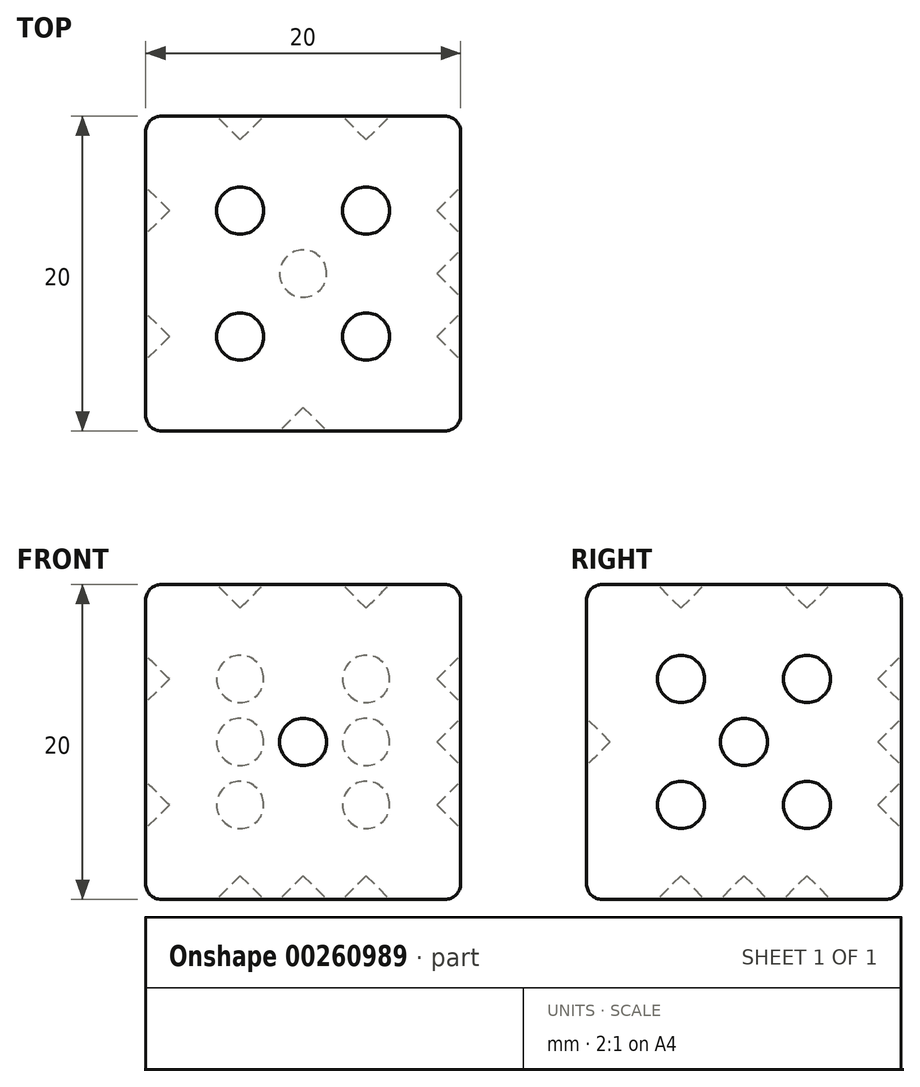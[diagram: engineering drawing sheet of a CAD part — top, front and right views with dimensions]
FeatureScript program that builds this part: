
annotation { "Feature Type Name" : "Feature", "Feature Type Description" : "" }
export const myFeature = defineFeature(function(context is Context, id is Id, definition is map)
    precondition{}
    {
        {
            var Q0;
            Q0=qCreatedBy(makeId("Top.planeOp"),FACE);
            var sketch = newSketch(context, id + "F0", { "sketchPlane" : qUnion([Q0])});
            skLineSegment(sketch, "E0.bottom", {"start": v(0, 0) * mm, "end": v(20, 0) * mm});
            skLineSegment(sketch, "E0.top", {"start": v(0, 20) * mm, "end": v(20, 20) * mm});
            skLineSegment(sketch, "E0.left", {"start": v(0, 0) * mm, "end": v(0, 20) * mm});
            skLineSegment(sketch, "E0.right", {"start": v(20, 0) * mm, "end": v(20, 20) * mm});
            skSolve(sketch);
        }
        {
            var Q0;
            Q0 = qSketchRegion(id + "F0", true);
            extrude(context, id + "F1", {"entities" : qUnion([Q0]), "depth" : 20 * mm});
        }
        {
            var Q0;
            Q0=makeQuery(id+"F1.opExtrude","SWEPT_FACE",FACE,{"disambiguationData":[OSD([sQuery(id+"F0.wireOp",EDGE,"E0.bottom")])]});
            var sketch = newSketch(context, id + "F2", { "sketchPlane" : qUnion([Q0])});
            skLineSegment(sketch, "E1.0", {"start": v(0, 20) * mm, "end": v(20, 20) * mm, "construction": true});
            skLineSegment(sketch, "E1.1", {"start": v(0, 0) * mm, "end": v(20, 0) * mm, "construction": true});
            skLineSegment(sketch, "E2", {"start": v(10, 20) * mm, "end": v(10, 0) * mm, "construction": true});
            skCircle(sketch, "E3", {"center": v(10, 10) * mm, "radius": 1.5 * mm});
            skSolve(sketch);
        }
        {
            var Q0;
            Q0=makeQuery(id+"F2.imprint","IMPRINT",FACE,{"disambiguationData":[TD([[makeQuery(id+"F2.imprint","IMPRINT",EDGE,{"derivedFrom":sQuery(id+"F2.wireOp",EDGE,"E3")}),1.0]])]});
            var Q1;
            Q1=sQuery(id+"F2.wireOp",EDGE,"E3");
            extrude(context, id + "F3", {"entities" : qUnion([Q0]), "operationType" : NewBodyOperationType.REMOVE, "surfaceEntities" : qUnion([Q1]), "oppositeDirection" : true, "depth" : 1.5 * mm});
        }
        {
            var Q0;
            Q0=makeQuery(id+"F1.opExtrude","CAP_FACE",FACE,{"disambiguationData":[OSD([sQuery(id+"F0.wireOp",EDGE,"E0.bottom"),sQuery(id+"F0.wireOp",EDGE,"E0.top"),sQuery(id+"F0.wireOp",EDGE,"E0.left"),sQuery(id+"F0.wireOp",EDGE,"E0.right")])],"isStart":false});
            var sketch = newSketch(context, id + "F4", { "sketchPlane" : qUnion([Q0])});
            skLineSegment(sketch, "E4.0", {"start": v(0, 20) * mm, "end": v(6, 20) * mm, "construction": true});
            skLineSegment(sketch, "E5", {"start": v(6, 20) * mm, "end": v(6, 14) * mm, "construction": true});
            skCircle(sketch, "E6", {"center": v(6, 14) * mm, "radius": 1.5 * mm});
            skCircle(sketch, "E7", {"center": v(6, 6) * mm, "radius": 1.5 * mm});
            skPoint(sketch, "E8.orphan", {"position": v(20, 0) * mm});
            skPoint(sketch, "E9.orphan", {"position": v(20, 20) * mm});
            skLineSegment(sketch, "E10", {"start": v(0, 0) * mm, "end": v(6, 0) * mm, "construction": true});
            skLineSegment(sketch, "E11", {"start": v(6, 0) * mm, "end": v(6, 6) * mm, "construction": true});
            skLineSegment(sketch, "E12.0", {"start": v(0, 20) * mm, "end": v(20, 20) * mm, "construction": true});
            skLineSegment(sketch, "E12.1", {"start": v(0, 0) * mm, "end": v(20, 0) * mm, "construction": true});
            skLineSegment(sketch, "E13", {"start": v(10, 20) * mm, "end": v(10, 0) * mm, "construction": true});
            skCircle(sketch, "E14.MirrorC", {"center": v(14, 6) * mm, "radius": 1.5 * mm});
            skCircle(sketch, "E15.MirrorC", {"center": v(14, 14) * mm, "radius": 1.5 * mm});
            skSolve(sketch);
        }
        {
            var Q0;
            Q0 = qSketchRegion(id + "F4", true);
            extrude(context, id + "F5", {"entities" : qUnion([Q0]), "operationType" : NewBodyOperationType.REMOVE, "oppositeDirection" : true, "depth" : 1.5 * mm});
        }
        {
            var Q0;
            Q0=makeQuery(id+"F1.opExtrude","SWEPT_FACE",FACE,{"disambiguationData":[OSD([sQuery(id+"F0.wireOp",EDGE,"E0.right")])]});
            var sketch = newSketch(context, id + "F6", { "sketchPlane" : qUnion([Q0])});
            skLineSegment(sketch, "E16", {"start": v(0, 20) * mm, "end": v(6, 20) * mm, "construction": true});
            skLineSegment(sketch, "E17", {"start": v(6, 20) * mm, "end": v(6, 14) * mm, "construction": true});
            skLineSegment(sketch, "E18", {"start": v(0, 0) * mm, "end": v(6, 0) * mm, "construction": true});
            skLineSegment(sketch, "E19", {"start": v(6, 0) * mm, "end": v(6, 6) * mm, "construction": true});
            skCircle(sketch, "E20", {"center": v(6, 14) * mm, "radius": 1.5 * mm});
            skCircle(sketch, "E21", {"center": v(6, 6) * mm, "radius": 1.5 * mm});
            skLineSegment(sketch, "E22", {"start": v(0, 20) * mm, "end": v(10, 20) * mm, "construction": true});
            skLineSegment(sketch, "E23", {"start": v(10, 20) * mm, "end": v(10, 0) * mm, "construction": true});
            skCircle(sketch, "E24.MirrorC", {"center": v(14, 6) * mm, "radius": 1.5 * mm});
            skCircle(sketch, "E25.MirrorC", {"center": v(14, 14) * mm, "radius": 1.5 * mm});
            skCircle(sketch, "E26", {"center": v(10, 10) * mm, "radius": 1.5 * mm});
            skSolve(sketch);
        }
        {
            var Q0;
            Q0 = qSketchRegion(id + "F6", true);
            extrude(context, id + "F7", {"entities" : qUnion([Q0]), "operationType" : NewBodyOperationType.REMOVE, "oppositeDirection" : true, "depth" : 1.5 * mm});
        }
        {
            var Q0;
            Q0=makeQuery(id+"F1.opExtrude","SWEPT_FACE",FACE,{"disambiguationData":[OSD([sQuery(id+"F0.wireOp",EDGE,"E0.top")])]});
            var sketch = newSketch(context, id + "F8", { "sketchPlane" : qUnion([Q0])});
            skLineSegment(sketch, "E27", {"start": v(-20, 20) * mm, "end": v(-14, 20) * mm, "construction": true});
            skLineSegment(sketch, "E28", {"start": v(-14, 20) * mm, "end": v(-14, 14) * mm, "construction": true});
            skLineSegment(sketch, "E29", {"start": v(-20, 0) * mm, "end": v(-14, 0) * mm, "construction": true});
            skLineSegment(sketch, "E30", {"start": v(-14, 0) * mm, "end": v(-14, 6) * mm, "construction": true});
            skLineSegment(sketch, "E31", {"start": v(-20, 20) * mm, "end": v(-14, 20) * mm});
            skLineSegment(sketch, "E32", {"start": v(-20, 0) * mm, "end": v(-14, 0) * mm});
            skCircle(sketch, "E33", {"center": v(-14, 14) * mm, "radius": 1.5 * mm});
            skCircle(sketch, "E34", {"center": v(-14, 6) * mm, "radius": 1.5 * mm});
            skLineSegment(sketch, "E35", {"start": v(-14, 14) * mm, "end": v(-14, 6) * mm, "construction": true});
            skCircle(sketch, "E36", {"center": v(-14, 10) * mm, "radius": 1.5 * mm});
            skLineSegment(sketch, "E37", {"start": v(-20, 20) * mm, "end": v(-10, 20) * mm, "construction": true});
            skLineSegment(sketch, "E38", {"start": v(-10, 20) * mm, "end": v(-10, 0) * mm, "construction": true});
            skCircle(sketch, "E39.MirrorC", {"center": v(-6, 14) * mm, "radius": 1.5 * mm});
            skCircle(sketch, "E40.MirrorC", {"center": v(-6, 10) * mm, "radius": 1.5 * mm});
            skCircle(sketch, "E41.MirrorC", {"center": v(-6, 6) * mm, "radius": 1.5 * mm});
            skSolve(sketch);
        }
        {
            var Q0;
            Q0 = qSketchRegion(id + "F8", true);
            extrude(context, id + "F9", {"entities" : qUnion([Q0]), "operationType" : NewBodyOperationType.REMOVE, "oppositeDirection" : true, "depth" : 1.5 * mm});
        }
        {
            var Q0;
            Q0=makeQuery(id+"F1.opExtrude","SWEPT_FACE",FACE,{"disambiguationData":[OSD([sQuery(id+"F0.wireOp",EDGE,"E0.left")])]});
            var sketch = newSketch(context, id + "F10", { "sketchPlane" : qUnion([Q0])});
            skLineSegment(sketch, "E42", {"start": v(-20, 20) * mm, "end": v(-14, 20) * mm, "construction": true});
            skLineSegment(sketch, "E43", {"start": v(-14, 20) * mm, "end": v(-14, 14) * mm, "construction": true});
            skCircle(sketch, "E44", {"center": v(-14, 14) * mm, "radius": 1.5 * mm});
            skLineSegment(sketch, "E45", {"start": v(-20, 0) * mm, "end": v(0, 20) * mm, "construction": true});
            skCircle(sketch, "E46.MirrorC", {"center": v(-6, 6) * mm, "radius": 1.5 * mm});
            skSolve(sketch);
        }
        {
            var Q0;
            Q0 = qSketchRegion(id + "F10", true);
            extrude(context, id + "F11", {"entities" : qUnion([Q0]), "operationType" : NewBodyOperationType.REMOVE, "oppositeDirection" : true, "depth" : 1.5 * mm});
        }
        {
            var Q0;
            Q0=makeQuery(id+"F1.opExtrude","CAP_FACE",FACE,{"disambiguationData":[OSD([sQuery(id+"F0.wireOp",EDGE,"E0.bottom"),sQuery(id+"F0.wireOp",EDGE,"E0.top"),sQuery(id+"F0.wireOp",EDGE,"E0.left"),sQuery(id+"F0.wireOp",EDGE,"E0.right")])],"isStart":true});
            var sketch = newSketch(context, id + "F12", { "sketchPlane" : qUnion([Q0])});
            skLineSegment(sketch, "E47", {"start": v(0, 0) * mm, "end": v(6, 0) * mm, "construction": true});
            skLineSegment(sketch, "E48", {"start": v(6, 0) * mm, "end": v(6, -6) * mm, "construction": true});
            skCircle(sketch, "E49", {"center": v(6, -6) * mm, "radius": 1.5 * mm});
            skLineSegment(sketch, "E50", {"start": v(0, -20) * mm, "end": v(20, 0) * mm, "construction": true});
            skCircle(sketch, "E51.MirrorC", {"center": v(14, -14) * mm, "radius": 1.5 * mm});
            skCircle(sketch, "E52", {"center": v(10, -10) * mm, "radius": 1.5 * mm});
            skSolve(sketch);
        }
        {
            var Q0;
            Q0 = qSketchRegion(id + "F12", true);
            extrude(context, id + "F13", {"entities" : qUnion([Q0]), "operationType" : NewBodyOperationType.REMOVE, "oppositeDirection" : true, "depth" : 1.5 * mm});
        }
        {
            var Q0;
            Q0=makeQuery(id+"F1.opExtrude","CAP_EDGE",EDGE,{"disambiguationData":[OSD([sQuery(id+"F0.wireOp",EDGE,"E0.left")])],"isStart":false});
            var Q1;
            Q1=makeQuery(id+"F1.opExtrude","CAP_EDGE",EDGE,{"disambiguationData":[OSD([sQuery(id+"F0.wireOp",EDGE,"E0.right")])],"isStart":false});
            var Q2;
            Q2=makeQuery(id+"F1.opExtrude","CAP_EDGE",EDGE,{"disambiguationData":[OSD([sQuery(id+"F0.wireOp",EDGE,"E0.bottom")])],"isStart":false});
            var Q3;
            Q3=makeQuery(id+"F1.opExtrude","CAP_EDGE",EDGE,{"disambiguationData":[OSD([sQuery(id+"F0.wireOp",EDGE,"E0.bottom")])],"isStart":true});
            var Q4;
            Q4=makeQuery(id+"F1.opExtrude","CAP_EDGE",EDGE,{"disambiguationData":[OSD([sQuery(id+"F0.wireOp",EDGE,"E0.left")])],"isStart":true});
            var Q5;
            Q5=makeQuery(id+"F1.opExtrude","CAP_EDGE",EDGE,{"disambiguationData":[OSD([sQuery(id+"F0.wireOp",EDGE,"E0.top")])],"isStart":true});
            var Q6;
            Q6=makeQuery(id+"F1.opExtrude","CAP_EDGE",EDGE,{"disambiguationData":[OSD([sQuery(id+"F0.wireOp",EDGE,"E0.top")])],"isStart":false});
            var Q7;
            Q7=makeQuery(id+"F1.opExtrude","SWEPT_EDGE",EDGE,{"disambiguationData":[OSD([sQuery(id+"F0.wireOp",EDGE,"E0.top"),sQuery(id+"F0.wireOp",EDGE,"E0.right")])]});
            var Q8;
            Q8=makeQuery(id+"F1.opExtrude","SWEPT_EDGE",EDGE,{"disambiguationData":[OSD([sQuery(id+"F0.wireOp",EDGE,"E0.top"),sQuery(id+"F0.wireOp",EDGE,"E0.left")])]});
            var Q9;
            Q9=makeQuery(id+"F1.opExtrude","SWEPT_EDGE",EDGE,{"disambiguationData":[OSD([sQuery(id+"F0.wireOp",EDGE,"E0.bottom"),sQuery(id+"F0.wireOp",EDGE,"E0.right")])]});
            var Q10;
            Q10=makeQuery(id+"F1.opExtrude","SWEPT_EDGE",EDGE,{"disambiguationData":[OSD([sQuery(id+"F0.wireOp",EDGE,"E0.bottom"),sQuery(id+"F0.wireOp",EDGE,"E0.left")])]});
            var Q11;
            Q11=makeQuery(id+"F1.opExtrude","CAP_EDGE",EDGE,{"disambiguationData":[OSD([sQuery(id+"F0.wireOp",EDGE,"E0.right")])],"isStart":true});
            fillet(context, id + "F14", {"entities" : qUnion([Q0, Q1, Q2, Q3, Q4, Q5, Q6, Q7, Q8, Q9, Q10, Q11]), "radius" : 1 * mm, "tangentPropagation" : true, "allowEdgeOverflow" : false});
        }
        {
            var Q0;
            Q0=makeQuery(id+"F3.boolean.opBoolean","COPY",EDGE,{"derivedFrom":makeQuery(id+"F3.opExtrude","CAP_EDGE",EDGE,{"disambiguationData":[OSD([sQuery(id+"F2.wireOp",EDGE,"E3")])],"isStart":false})});
            var Q1;
            Q1=makeQuery(id+"F5.boolean.opBoolean","COPY",EDGE,{"derivedFrom":makeQuery(id+"F5.opExtrude","CAP_EDGE",EDGE,{"disambiguationData":[OSD([sQuery(id+"F4.wireOp",EDGE,"E6")])],"isStart":false})});
            var Q2;
            Q2=makeQuery(id+"F5.boolean.opBoolean","COPY",EDGE,{"derivedFrom":makeQuery(id+"F5.opExtrude","CAP_EDGE",EDGE,{"disambiguationData":[OSD([sQuery(id+"F4.wireOp",EDGE,"E7")])],"isStart":false})});
            var Q3;
            Q3=makeQuery(id+"F5.boolean.opBoolean","COPY",EDGE,{"derivedFrom":makeQuery(id+"F5.opExtrude","CAP_EDGE",EDGE,{"disambiguationData":[OSD([sQuery(id+"F4.wireOp",EDGE,"E14.MirrorC")])],"isStart":false})});
            var Q4;
            Q4=makeQuery(id+"F5.boolean.opBoolean","COPY",EDGE,{"derivedFrom":makeQuery(id+"F5.opExtrude","CAP_EDGE",EDGE,{"disambiguationData":[OSD([sQuery(id+"F4.wireOp",EDGE,"E15.MirrorC")])],"isStart":false})});
            var Q5;
            Q5=makeQuery(id+"F7.boolean.opBoolean","COPY",FACE,{"derivedFrom":makeQuery(id+"F7.opExtrude","CAP_FACE",FACE,{"disambiguationData":[OSD([sQuery(id+"F6.wireOp",EDGE,"E21")])],"isStart":false})});
            var Q6;
            Q6=makeQuery(id+"F7.boolean.opBoolean","COPY",FACE,{"derivedFrom":makeQuery(id+"F7.opExtrude","CAP_FACE",FACE,{"disambiguationData":[OSD([sQuery(id+"F6.wireOp",EDGE,"E20")])],"isStart":false})});
            var Q7;
            Q7=makeQuery(id+"F7.boolean.opBoolean","COPY",FACE,{"derivedFrom":makeQuery(id+"F7.opExtrude","CAP_FACE",FACE,{"disambiguationData":[OSD([sQuery(id+"F6.wireOp",EDGE,"E25.MirrorC")])],"isStart":false})});
            var Q8;
            Q8=makeQuery(id+"F7.boolean.opBoolean","COPY",FACE,{"derivedFrom":makeQuery(id+"F7.opExtrude","CAP_FACE",FACE,{"disambiguationData":[OSD([sQuery(id+"F6.wireOp",EDGE,"E24.MirrorC")])],"isStart":false})});
            var Q9;
            Q9=makeQuery(id+"F7.boolean.opBoolean","COPY",FACE,{"derivedFrom":makeQuery(id+"F7.opExtrude","CAP_FACE",FACE,{"disambiguationData":[OSD([sQuery(id+"F6.wireOp",EDGE,"E26")])],"isStart":false})});
            var Q10;
            Q10=makeQuery(id+"F9.boolean.opBoolean","COPY",FACE,{"derivedFrom":makeQuery(id+"F9.opExtrude","CAP_FACE",FACE,{"disambiguationData":[OSD([sQuery(id+"F8.wireOp",EDGE,"E33")])],"isStart":false})});
            var Q11;
            Q11=makeQuery(id+"F9.boolean.opBoolean","COPY",FACE,{"derivedFrom":makeQuery(id+"F9.opExtrude","CAP_FACE",FACE,{"disambiguationData":[OSD([sQuery(id+"F8.wireOp",EDGE,"E36")])],"isStart":false})});
            var Q12;
            Q12=makeQuery(id+"F9.boolean.opBoolean","COPY",EDGE,{"derivedFrom":makeQuery(id+"F9.opExtrude","CAP_EDGE",EDGE,{"disambiguationData":[OSD([sQuery(id+"F8.wireOp",EDGE,"E34")])],"isStart":false})});
            var Q13;
            Q13=makeQuery(id+"F9.boolean.opBoolean","COPY",FACE,{"derivedFrom":makeQuery(id+"F9.opExtrude","CAP_FACE",FACE,{"disambiguationData":[OSD([sQuery(id+"F8.wireOp",EDGE,"E41.MirrorC")])],"isStart":false})});
            var Q14;
            Q14=makeQuery(id+"F9.boolean.opBoolean","COPY",FACE,{"derivedFrom":makeQuery(id+"F9.opExtrude","CAP_FACE",FACE,{"disambiguationData":[OSD([sQuery(id+"F8.wireOp",EDGE,"E40.MirrorC")])],"isStart":false})});
            var Q15;
            Q15=makeQuery(id+"F9.boolean.opBoolean","COPY",FACE,{"derivedFrom":makeQuery(id+"F9.opExtrude","CAP_FACE",FACE,{"disambiguationData":[OSD([sQuery(id+"F8.wireOp",EDGE,"E39.MirrorC")])],"isStart":false})});
            var Q16;
            Q16=makeQuery(id+"F11.boolean.opBoolean","COPY",EDGE,{"derivedFrom":makeQuery(id+"F11.opExtrude","CAP_EDGE",EDGE,{"disambiguationData":[OSD([sQuery(id+"F10.wireOp",EDGE,"E44")])],"isStart":false})});
            var Q17;
            Q17=makeQuery(id+"F11.boolean.opBoolean","COPY",FACE,{"derivedFrom":makeQuery(id+"F11.opExtrude","CAP_FACE",FACE,{"disambiguationData":[OSD([sQuery(id+"F10.wireOp",EDGE,"E46.MirrorC")])],"isStart":false})});
            var Q18;
            Q18=makeQuery(id+"F13.boolean.opBoolean","COPY",FACE,{"derivedFrom":makeQuery(id+"F13.opExtrude","CAP_FACE",FACE,{"disambiguationData":[OSD([sQuery(id+"F12.wireOp",EDGE,"E49")])],"isStart":false})});
            var Q19;
            Q19=makeQuery(id+"F13.boolean.opBoolean","COPY",FACE,{"derivedFrom":makeQuery(id+"F13.opExtrude","CAP_FACE",FACE,{"disambiguationData":[OSD([sQuery(id+"F12.wireOp",EDGE,"E52")])],"isStart":false})});
            var Q20;
            Q20=makeQuery(id+"F13.boolean.opBoolean","COPY",FACE,{"derivedFrom":makeQuery(id+"F13.opExtrude","CAP_FACE",FACE,{"disambiguationData":[OSD([sQuery(id+"F12.wireOp",EDGE,"E51.MirrorC")])],"isStart":false})});
            chamfer(context, id + "F15", {"entities" : qUnion([Q0, Q1, Q2, Q3, Q4, Q5, Q6, Q7, Q8, Q9, Q10, Q11, Q12, Q13, Q14, Q15, Q16, Q17, Q18, Q19, Q20]), "width" : 1.5 * mm, "tangentPropagation" : true});
        }
    });
